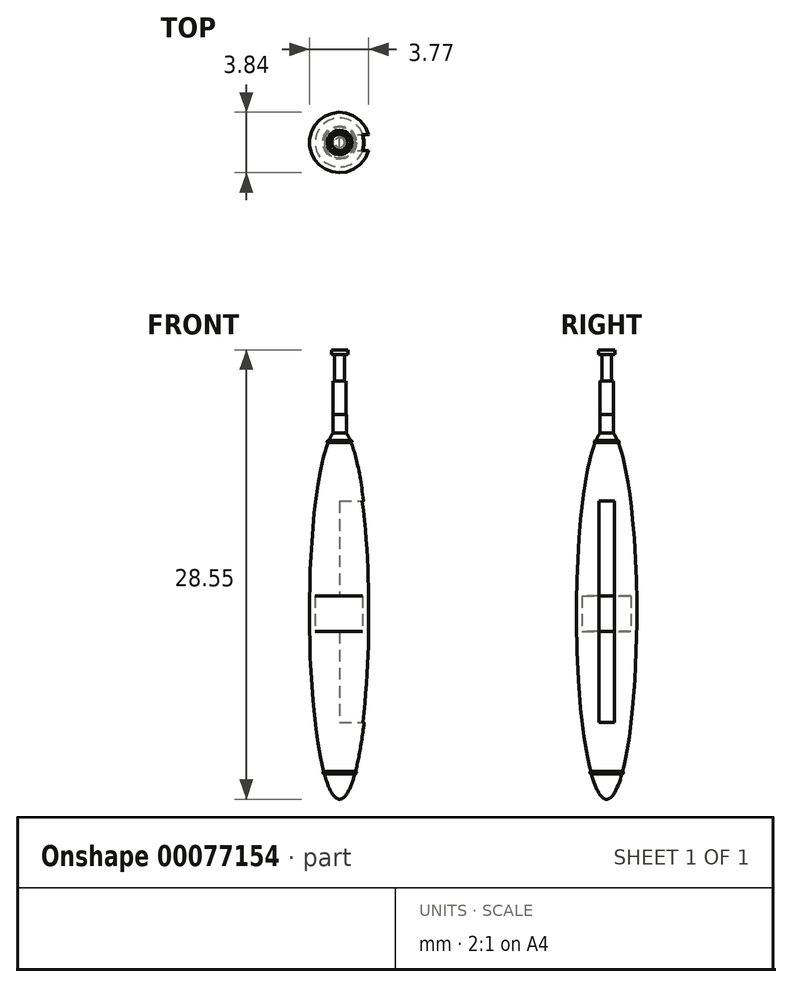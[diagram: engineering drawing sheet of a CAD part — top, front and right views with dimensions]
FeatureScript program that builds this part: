
annotation { "Feature Type Name" : "Feature", "Feature Type Description" : "" }
export const myFeature = defineFeature(function(context is Context, id is Id, definition is map)
    precondition{}
    {
        {
            var Q0;
            Q0=qCreatedBy(makeId("Front.planeOp"),FACE);
            var sketch = newSketch(context, id + "F0", { "sketchPlane" : qUnion([Q0])});
            skEllipticalArc(sketch, "E0", {});
            skLineSegment(sketch, "E1", {"start": v(0, 11.78) * mm, "end": v(0, -11.78) * mm});
            skLineSegment(sketch, "E2.bottom", {"start": v(-0.43, 11.48) * mm, "end": v(-0.43, 11.48) * mm});
            skLineSegment(sketch, "E2.top", {"start": v(-0.42, 12.66) * mm, "end": v(-0.43, 12.66) * mm});
            skLineSegment(sketch, "E2.left", {"start": v(0, 11.48) * mm, "end": v(0, 12.66) * mm});
            skLineSegment(sketch, "E2.right", {"start": v(-0.43, 11.48) * mm, "end": v(-0.43, 12.66) * mm});
            skLineSegment(sketch, "E3.left", {"start": v(0, 12.66) * mm, "end": v(0, 14.78) * mm});
            skLineSegment(sketch, "E3.right", {"start": v(-0.42, 12.66) * mm, "end": v(-0.42, 14.78) * mm});
            skLineSegment(sketch, "E4.left", {"start": v(0, 14.78) * mm, "end": v(0, 16.48) * mm});
            skLineSegment(sketch, "E4.right", {"start": v(-0.3, 14.78) * mm, "end": v(-0.3, 16.48) * mm});
            skLineSegment(sketch, "E5", {"start": v(-0.3, 14.78) * mm, "end": v(-0.42, 14.78) * mm});
            skArc(sketch, "E6", {"start": v(-0.68, 11) * mm, "mid": v(-0.78, 10.97) * mm, "end": v(-0.74, 10.87) * mm});
            skEllipticalArc(sketch, "E7.trimOffspring", {});
            skArc(sketch, "E8", {"start": v(-1, -10.01) * mm, "mid": v(-1.06, -10.1) * mm, "end": v(-0.97, -10.16) * mm});
            skEllipticalArc(sketch, "E9.trimOffspring", {});
            skLineSegment(sketch, "E10.bottom", {"start": v(-0.3, 16.48) * mm, "end": v(-0.52, 16.48) * mm});
            skLineSegment(sketch, "E10.top", {"start": v(0, 16.77) * mm, "end": v(-0.52, 16.77) * mm});
            skLineSegment(sketch, "E10.left", {"start": v(0, 16.48) * mm, "end": v(0, 16.77) * mm});
            skLineSegment(sketch, "E10.right", {"start": v(-0.52, 16.48) * mm, "end": v(-0.52, 16.77) * mm});
            const initialGuessF0  = {"E0": [0, 0, 0, 1, 0.011777514631263973, 0.001916683178784572, 0.22421039553335678, 0.36366982071250753], "E7.trimOffspring": [0, 0, 0, 1, 0.011777514631263973, 0.001916683178784572, 0.3950853549318617, 2.587374773479048], "E9.trimOffspring": [0, 0, 0, 1, 0.011777514631263973, 0.001916683178784572, 2.6108752879956154, 3.141592653589793]};
            skSetInitialGuess(sketch, initialGuessF0);
            skSolve(sketch);
        }
        {
            var Q0;
            Q0=makeQuery(id+"F0.imprint","IMPRINT",FACE,{"disambiguationData":[TD([[makeQuery(id+"F0.imprint","IMPRINT",EDGE,{"derivedFrom":sQuery(id+"F0.wireOp",EDGE,"E0")}),1.0]])]});
            var Q1;
            Q1=sQuery(id+"F0.wireOp",EDGE,"E1");
            revolve(context, id + "F1", {"entities" : qUnion([Q0]), "axis" : qUnion([Q1]), "revolveType" : RevolveType.FULL});
        }
        {
            var Q0;
            Q0=qCreatedBy(makeId("Front.planeOp"),FACE);
            var sketch = newSketch(context, id + "F2", { "sketchPlane" : qUnion([Q0])});
            skLineSegment(sketch, "E11.top", {"start": v(0, 1.13) * mm, "end": v(-1.55, 1.13) * mm});
            skLineSegment(sketch, "E11.left", {"start": v(0, 0) * mm, "end": v(0, 1.13) * mm});
            skLineSegment(sketch, "E11.right", {"start": v(-1.55, 0) * mm, "end": v(-1.55, 1.13) * mm});
            skLineSegment(sketch, "E12.MirrorCS", {"start": v(-1.55, 0) * mm, "end": v(-1.55, -1.13) * mm});
            skLineSegment(sketch, "E13.MirrorCS", {"start": v(0, -1.13) * mm, "end": v(-1.55, -1.13) * mm});
            skLineSegment(sketch, "E14.MirrorCS", {"start": v(0, 0) * mm, "end": v(0, -1.13) * mm});
            skSolve(sketch);
        }
        {
            var Q0;
            Q0=qCreatedBy(makeId("Front.planeOp"),FACE);
            var sketch = newSketch(context, id + "F3", { "sketchPlane" : qUnion([Q0])});
            skLineSegment(sketch, "E15.bottom", {"start": v(0, 7.17) * mm, "end": v(4.16, 7.17) * mm});
            skLineSegment(sketch, "E15.top", {"start": v(0, -6.88) * mm, "end": v(4.16, -6.88) * mm});
            skLineSegment(sketch, "E15.left", {"start": v(0, 7.17) * mm, "end": v(0, -6.88) * mm});
            skLineSegment(sketch, "E15.right", {"start": v(4.16, 7.17) * mm, "end": v(4.16, -6.88) * mm});
            skSolve(sketch);
        }
        {
            var Q0;
            Q0=makeQuery(id+"F3.imprint","IMPRINT",FACE,{"disambiguationData":[TD([[makeQuery(id+"F3.imprint","IMPRINT",EDGE,{"derivedFrom":sQuery(id+"F3.wireOp",EDGE,"E15.bottom")}),-1.0]])]});
            extrude(context, id + "F4", {"entities" : qUnion([Q0]), "operationType" : NewBodyOperationType.REMOVE, "depth" : 1 * mm, "offsetDistance" : 25 * mm, "symmetric" : true});
        }
        {
            var Q0;
            Q0 = qSketchRegion(id + "F2", true);
            var Q1;
            Q1=sQuery(id+"F2.wireOp",EDGE,"E14.MirrorCS");
            revolve(context, id + "F5", {"operationType" : NewBodyOperationType.REMOVE, "entities" : qUnion([Q0]), "axis" : qUnion([Q1]), "revolveType" : RevolveType.FULL, "oppositeDirection" : true});
        }
    });
